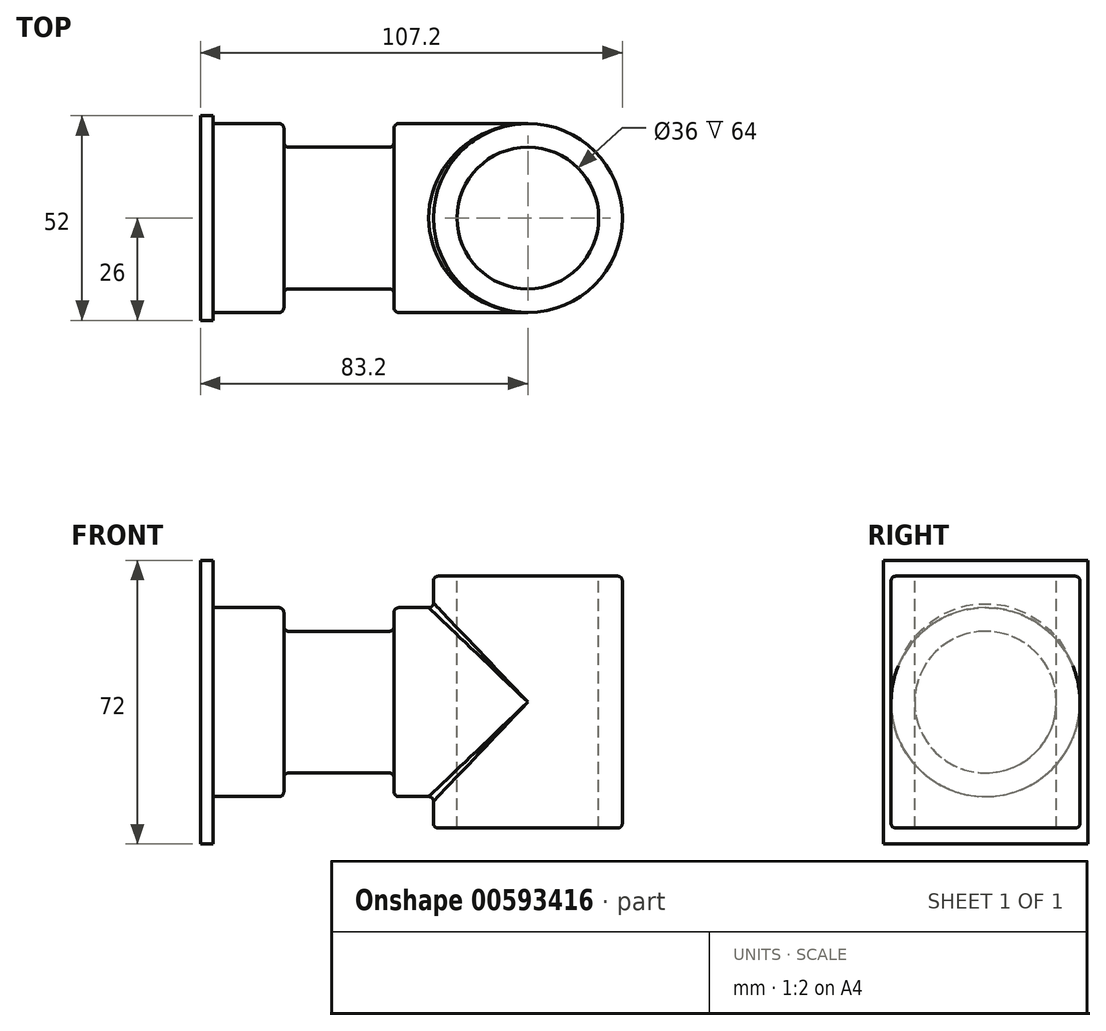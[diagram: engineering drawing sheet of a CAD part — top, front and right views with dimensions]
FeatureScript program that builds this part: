
annotation { "Feature Type Name" : "Feature", "Feature Type Description" : "" }
export const myFeature = defineFeature(function(context is Context, id is Id, definition is map)
    precondition{}
    {
        {
            var Q0;
            Q0=qCreatedBy(makeId("Front.planeOp"),FACE);
            var sketch = newSketch(context, id + "F0", { "sketchPlane" : qUnion([Q0])});
            skLineSegment(sketch, "E0", {"start": v(-80, 24) * mm, "end": v(-63.2, 24) * mm});
            skLineSegment(sketch, "E1", {"start": v(-62, 22.8) * mm, "end": v(-62, 18) * mm});
            skLineSegment(sketch, "E2", {"start": v(-62, 18) * mm, "end": v(-34, 18) * mm});
            skLineSegment(sketch, "E3", {"start": v(-34, 18) * mm, "end": v(-34, 22.8) * mm});
            skLineSegment(sketch, "E4", {"start": v(-32.8, 24) * mm, "end": v(0, 24) * mm});
            skLineSegment(sketch, "E5", {"start": v(0, 24) * mm, "end": v(0, 0) * mm});
            skLineSegment(sketch, "E6", {"start": v(-80, 24) * mm, "end": v(-80, 0) * mm});
            skLineSegment(sketch, "E7", {"start": v(-80, 0) * mm, "end": v(0, 0) * mm});
            skPoint(sketch, "E8.visualSharp", {"position": v(-80, 24) * mm});
            skPoint(sketch, "E9.visualSharp", {"position": v(-62, 24) * mm});
            skArc(sketch, "E9.filletArc", {"start": v(-62, 22.8) * mm, "mid": v(-62.35, 23.65) * mm, "end": v(-63.2, 24) * mm});
            skPoint(sketch, "E10.visualSharp", {"position": v(-34, 24) * mm});
            skArc(sketch, "E10.filletArc", {"start": v(-32.8, 24) * mm, "mid": v(-33.65, 23.65) * mm, "end": v(-34, 22.8) * mm});
            skPoint(sketch, "E11.visualSharp", {"position": v(0, 24) * mm});
            skSolve(sketch);
        }
        {
            var Q0;
            Q0 = qSketchRegion(id + "F0", true);
            var Q1;
            Q1=sQuery(id+"F0.wireOp",EDGE,"E7");
            revolve(context, id + "F1", {"entities" : qUnion([Q0]), "axis" : qUnion([Q1]), "revolveType" : RevolveType.FULL});
        }
        {
            var Q0;
            Q0=qCreatedBy(makeId("Front.planeOp"),FACE);
            var sketch = newSketch(context, id + "F2", { "sketchPlane" : qUnion([Q0])});
            skLineSegment(sketch, "E12.bottom", {"start": v(-22.8, 32) * mm, "end": v(0, 32) * mm});
            skLineSegment(sketch, "E12.top", {"start": v(-22.8, -32) * mm, "end": v(0, -32) * mm});
            skLineSegment(sketch, "E12.left", {"start": v(-24, 30.8) * mm, "end": v(-24, -30.8) * mm});
            skLineSegment(sketch, "E12.right", {"start": v(0, 32) * mm, "end": v(0, -32) * mm});
            skPoint(sketch, "E13.visualSharp", {"position": v(-24, 32) * mm});
            skArc(sketch, "E13.filletArc", {"start": v(-22.8, 32) * mm, "mid": v(-23.65, 31.65) * mm, "end": v(-24, 30.8) * mm});
            skPoint(sketch, "E14.visualSharp", {"position": v(-24, -32) * mm});
            skArc(sketch, "E14.filletArc", {"start": v(-24, -30.8) * mm, "mid": v(-23.65, -31.65) * mm, "end": v(-22.8, -32) * mm});
            skSolve(sketch);
        }
        {
            var Q0;
            Q0 = qSketchRegion(id + "F2", true);
            var Q1;
            Q1=sQuery(id+"F2.wireOp",EDGE,"E12.right");
            revolve(context, id + "F3", {"operationType" : NewBodyOperationType.ADD, "entities" : qUnion([Q0]), "axis" : qUnion([Q1]), "revolveType" : RevolveType.FULL});
        }
        {
            var Q0;
            Q0=makeQuery(id+"F1.opRevolve","SWEPT_FACE",FACE,{"disambiguationData":[OSD([sQuery(id+"F0.wireOp",EDGE,"E6")])]});
            var sketch = newSketch(context, id + "F4", { "sketchPlane" : qUnion([Q0])});
            skLineSegment(sketch, "E15.bottom", {"start": v(-26, 36) * mm, "end": v(26, 36) * mm});
            skLineSegment(sketch, "E15.top", {"start": v(-26, -36) * mm, "end": v(26, -36) * mm});
            skLineSegment(sketch, "E15.left", {"start": v(-26, 36) * mm, "end": v(-26, -36) * mm});
            skLineSegment(sketch, "E15.right", {"start": v(26, 36) * mm, "end": v(26, -36) * mm});
            skPoint(sketch, "E15.middle", {"position": v(0, 0) * mm});
            skSolve(sketch);
        }
        {
            var Q0;
            Q0 = qSketchRegion(id + "F4", true);
            extrude(context, id + "F5", {"entities" : qUnion([Q0]), "operationType" : NewBodyOperationType.ADD, "depth" : 3.2 * mm, "offsetDistance" : 25 * mm});
        }
        {
            var Q0;
            Q0=makeQuery(id+"F1.opRevolve","SWEPT_EDGE",EDGE,{"disambiguationData":[OSD([sQuery(id+"F0.wireOp",EDGE,"E0"),sQuery(id+"F0.wireOp",EDGE,"E6")])]});
            var Q1;
            Q1=makeQuery(id+"F1.opRevolve","SWEPT_EDGE",EDGE,{"disambiguationData":[OSD([sQuery(id+"F0.wireOp",EDGE,"E2"),sQuery(id+"F0.wireOp",EDGE,"E3")])]});
            var Q2;
            Q2=makeQuery(id+"F1.opRevolve","SWEPT_EDGE",EDGE,{"disambiguationData":[OSD([sQuery(id+"F0.wireOp",EDGE,"E1"),sQuery(id+"F0.wireOp",EDGE,"E2")])]});
            var Q3;
            Q3=makeQuery(id+"F3.boolean.opBoolean","INTERSECT",EDGE,{"disambiguationData":[OD(1.0)],"derivedFrom":[makeQuery(id+"F1.opRevolve","SWEPT_FACE",FACE,{"disambiguationData":[OSD([sQuery(id+"F0.wireOp",EDGE,"E4")])]}),makeQuery(id+"F3.opRevolve","SWEPT_FACE",FACE,{"disambiguationData":[OSD([sQuery(id+"F2.wireOp",EDGE,"E12.left")])]})]});
            var Q4;
            Q4=makeQuery(id+"F3.boolean.opBoolean","INTERSECT",EDGE,{"disambiguationData":[OD(0.0)],"derivedFrom":[makeQuery(id+"F1.opRevolve","SWEPT_FACE",FACE,{"disambiguationData":[OSD([sQuery(id+"F0.wireOp",EDGE,"E4")])]}),makeQuery(id+"F3.opRevolve","SWEPT_FACE",FACE,{"disambiguationData":[OSD([sQuery(id+"F2.wireOp",EDGE,"E12.left")])]})]});
            fillet(context, id + "F6", {"entities" : qUnion([Q0, Q1, Q2, Q3, Q4]), "radius" : 1.2 * mm, "tangentPropagation" : true, "allowEdgeOverflow" : false});
        }
        {
            var Q0;
            Q0=makeQuery(id+"F3.opRevolve","SWEPT_FACE",FACE,{"disambiguationData":[OSD([sQuery(id+"F2.wireOp",EDGE,"E12.bottom")])]});
            var sketch = newSketch(context, id + "F7", { "sketchPlane" : qUnion([Q0])});
            skCircle(sketch, "E16", {"center": v(0, 0) * mm, "radius": 18 * mm});
            skSolve(sketch);
        }
        {
            var Q0;
            Q0 = qSketchRegion(id + "F7", true);
            extrude(context, id + "F8", {"entities" : qUnion([Q0]), "operationType" : NewBodyOperationType.REMOVE, "endBound" : BoundingType.THROUGH_ALL, "oppositeDirection" : true, "depth" : 25 * mm, "offsetDistance" : 25 * mm});
        }
    });
